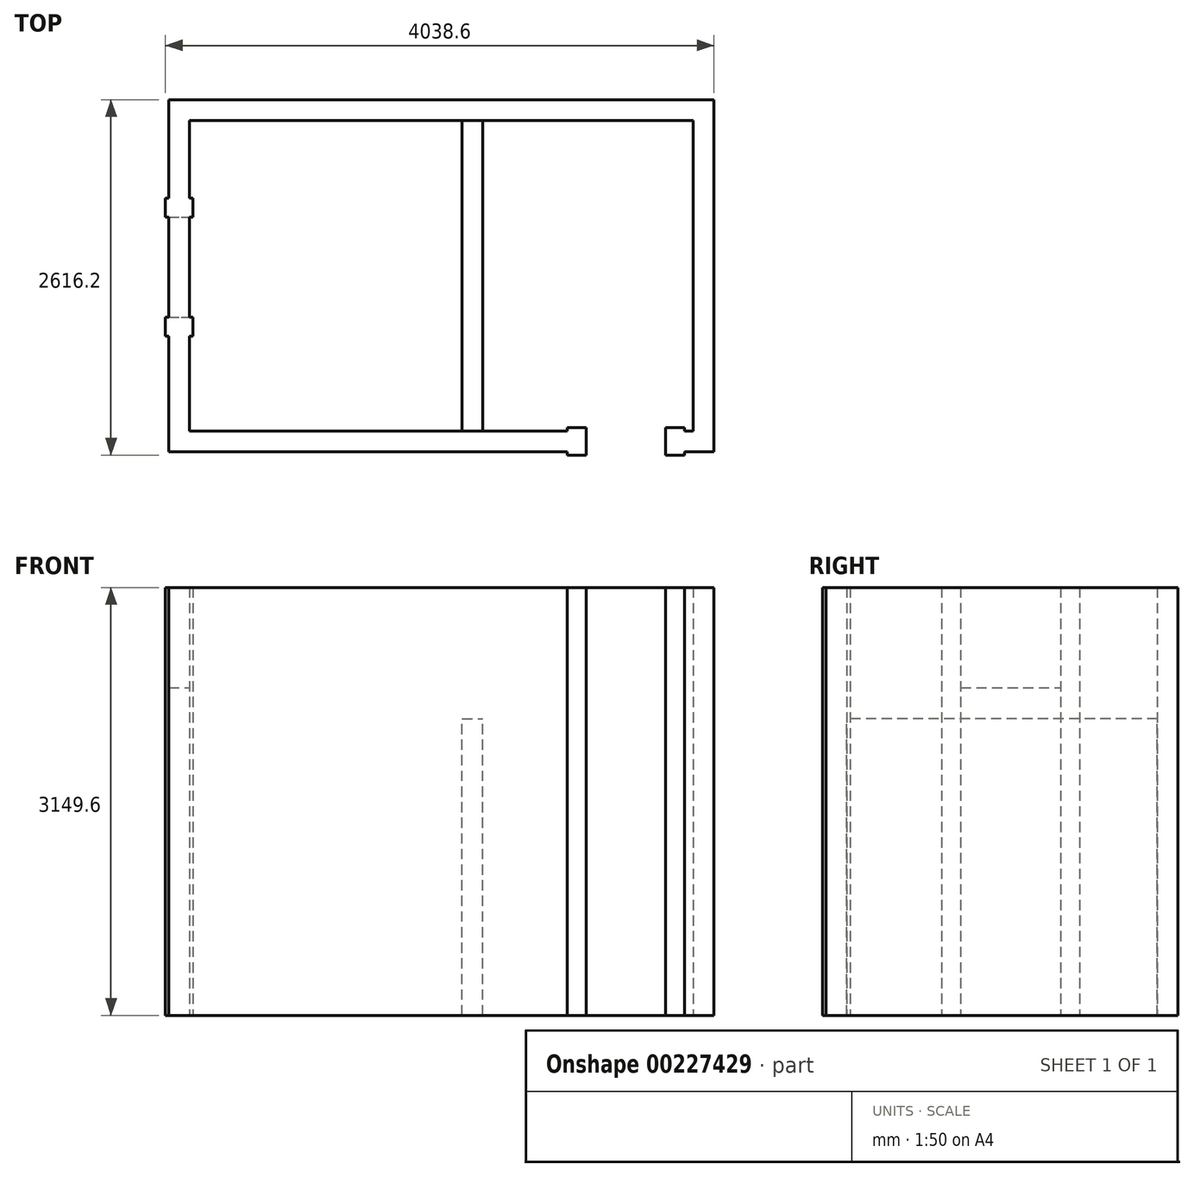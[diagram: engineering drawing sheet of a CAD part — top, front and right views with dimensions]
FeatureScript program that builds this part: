
annotation { "Feature Type Name" : "Feature", "Feature Type Description" : "" }
export const myFeature = defineFeature(function(context is Context, id is Id, definition is map)
    precondition{}
    {
        {
            var Q0;
            Q0=qCreatedBy(makeId("Top.planeOp"),FACE);
            var sketch = newSketch(context, id + "F0", { "sketchPlane" : qUnion([Q0])});
            skLineSegment(sketch, "E0.bottom", {"start": v(0, 0) * mm, "end": v(3708.4, 0) * mm});
            skLineSegment(sketch, "E0.top", {"start": v(0, 2286) * mm, "end": v(3708.4, 2286) * mm});
            skLineSegment(sketch, "E0.left", {"start": v(0, 0) * mm, "end": v(0, 2286) * mm});
            skLineSegment(sketch, "E0.right", {"start": v(3708.4, 0) * mm, "end": v(3708.4, 2286) * mm});
            skLineSegment(sketch, "E1.bottom", {"start": v(-152.4, -152.4) * mm, "end": v(3860.8, -152.4) * mm});
            skLineSegment(sketch, "E1.top", {"start": v(-152.4, 2438.4) * mm, "end": v(3860.8, 2438.4) * mm});
            skLineSegment(sketch, "E1.left", {"start": v(-152.4, -152.4) * mm, "end": v(-152.4, 2438.4) * mm});
            skLineSegment(sketch, "E1.right", {"start": v(3860.8, -152.4) * mm, "end": v(3860.8, 2438.4) * mm});
            skLineSegment(sketch, "E2.bottom", {"start": v(-152.4, 1574.8) * mm, "end": v(0, 1574.8) * mm});
            skLineSegment(sketch, "E2.top", {"start": v(-152.4, 838.2) * mm, "end": v(0, 838.2) * mm});
            skLineSegment(sketch, "E2.left", {"start": v(-152.4, 1574.8) * mm, "end": v(-152.4, 838.2) * mm});
            skLineSegment(sketch, "E2.right", {"start": v(0, 1574.8) * mm, "end": v(0, 838.2) * mm});
            skLineSegment(sketch, "E3.top", {"start": v(2921, -152.4) * mm, "end": v(3505.2, -152.4) * mm});
            skLineSegment(sketch, "E3.left", {"start": v(2921, 0) * mm, "end": v(2921, -152.4) * mm});
            skLineSegment(sketch, "E3.right", {"start": v(3505.2, 0) * mm, "end": v(3505.2, -152.4) * mm});
            skLineSegment(sketch, "E4.bottom", {"start": v(-177.8, 1714.5) * mm, "end": v(25.4, 1714.5) * mm});
            skLineSegment(sketch, "E4.top", {"start": v(-177.8, 1574.8) * mm, "end": v(25.4, 1574.8) * mm});
            skLineSegment(sketch, "E4.left", {"start": v(-177.8, 1714.5) * mm, "end": v(-177.8, 1574.8) * mm});
            skLineSegment(sketch, "E4.right", {"start": v(25.4, 1714.5) * mm, "end": v(25.4, 1574.8) * mm});
            skLineSegment(sketch, "E5.bottom", {"start": v(-177.8, 838.2) * mm, "end": v(25.4, 838.2) * mm});
            skLineSegment(sketch, "E5.top", {"start": v(-177.8, 698.5) * mm, "end": v(25.4, 698.5) * mm});
            skLineSegment(sketch, "E5.left", {"start": v(-177.8, 838.2) * mm, "end": v(-177.8, 698.5) * mm});
            skLineSegment(sketch, "E5.right", {"start": v(25.4, 838.2) * mm, "end": v(25.4, 698.5) * mm});
            skLineSegment(sketch, "E6.top", {"start": v(2692.4, 25.4) * mm, "end": v(2844.8, 25.4) * mm});
            skLineSegment(sketch, "E7.bottom", {"start": v(2781.3, 25.4) * mm, "end": v(2921, 25.4) * mm});
            skLineSegment(sketch, "E7.top", {"start": v(2781.3, -177.8) * mm, "end": v(2921, -177.8) * mm});
            skLineSegment(sketch, "E7.left", {"start": v(2781.3, 25.4) * mm, "end": v(2781.3, -177.8) * mm});
            skLineSegment(sketch, "E7.right", {"start": v(2921, 25.4) * mm, "end": v(2921, -177.8) * mm});
            skLineSegment(sketch, "E8.bottom", {"start": v(3505.2, 25.4) * mm, "end": v(3644.9, 25.4) * mm});
            skLineSegment(sketch, "E8.top", {"start": v(3505.2, -177.8) * mm, "end": v(3644.9, -177.8) * mm});
            skLineSegment(sketch, "E8.left", {"start": v(3505.2, 25.4) * mm, "end": v(3505.2, -177.8) * mm});
            skLineSegment(sketch, "E8.right", {"start": v(3644.9, 25.4) * mm, "end": v(3644.9, -177.8) * mm});
            skLineSegment(sketch, "E9", {"start": v(2006.6, 2286) * mm, "end": v(2006.6, 0) * mm});
            skLineSegment(sketch, "E10", {"start": v(2159, 2286) * mm, "end": v(2159, 0) * mm});
            skSolve(sketch);
        }
        {
            var Q0;
            {var subQ3=sQuery(id+"F0.wireOp",EDGE,"E0.top");Q0=makeQuery(id+"F0.imprint","IMPRINT",FACE,{"disambiguationData":[TD([[makeQuery(id+"F0.imprint","IMPRINT",EDGE,{"derivedFrom":subQ3}),1.0]])]});}
            var Q1;
            {var subQ3=sQuery(id+"F0.wireOp",EDGE,"E2.top");Q1=makeQuery(id+"F0.imprint","IMPRINT",FACE,{"disambiguationData":[TD([[makeQuery(id+"F0.imprint","IMPRINT",EDGE,{"derivedFrom":subQ3}),-1.0]])]});}
            var Q2;
            {var subQ5=sQuery(id+"F0.wireOp",EDGE,"E8.bottom");Q2=makeQuery(id+"F0.imprint","IMPRINT",FACE,{"disambiguationData":[TD([[makeQuery(id+"F0.imprint","IMPRINT",EDGE,{"derivedFrom":subQ5}),-1.0]])]});}
            var Q3;
            {var subQ0=sQuery(id+"F0.wireOp",EDGE,"E8.left");var subQ1=sQuery(id+"F0.wireOp",EDGE,"E0.bottom");var subQ2=makeQuery(id+"F0.imprint","INTERSECT",VERTEX,{"derivedFrom":[subQ1,subQ0]});Q3=makeQuery(id+"F0.imprint","IMPRINT",FACE,{"disambiguationData":[TD([[makeQuery(id+"F0.imprint","IMPRINT",EDGE,{"disambiguationData":[TD([[subQ2,-1.0]])],"derivedFrom":subQ1}),-1.0]])]});}
            var Q4;
            {var subQ5=sQuery(id+"F0.wireOp",EDGE,"E8.top");Q4=makeQuery(id+"F0.imprint","IMPRINT",FACE,{"disambiguationData":[TD([[makeQuery(id+"F0.imprint","IMPRINT",EDGE,{"derivedFrom":subQ5}),1.0]])]});}
            var Q5;
            {var subQ5=sQuery(id+"F0.wireOp",EDGE,"E7.top");Q5=makeQuery(id+"F0.imprint","IMPRINT",FACE,{"disambiguationData":[TD([[makeQuery(id+"F0.imprint","IMPRINT",EDGE,{"derivedFrom":subQ5}),1.0]])]});}
            var Q6;
            {var subQ0=sQuery(id+"F0.wireOp",EDGE,"E7.left");var subQ1=sQuery(id+"F0.wireOp",EDGE,"E0.bottom");var subQ2=makeQuery(id+"F0.imprint","INTERSECT",VERTEX,{"derivedFrom":[subQ1,subQ0]});Q6=makeQuery(id+"F0.imprint","IMPRINT",FACE,{"disambiguationData":[TD([[makeQuery(id+"F0.imprint","IMPRINT",EDGE,{"disambiguationData":[TD([[subQ2,-1.0]])],"derivedFrom":subQ1}),-1.0]])]});}
            var Q7;
            {var subQ1=sQuery(id+"F0.wireOp",EDGE,"E7.bottom");var subQ7=makeQuery(id+"F0.imprint","IMPRINT",VERTEX,{"derivedFrom":subQ1});Q7=makeQuery(id+"F0.imprint","IMPRINT",FACE,{"disambiguationData":[TD([[makeQuery(id+"F0.imprint","IMPRINT",EDGE,{"disambiguationData":[TD([[subQ7,1.0]])],"derivedFrom":subQ1}),-1.0]])]});}
            var Q8;
            {var subQ5=sQuery(id+"F0.wireOp",EDGE,"E0.left");var subQ6=sQuery(id+"F0.wireOp",EDGE,"E0.bottom");var subQ7=makeQuery(id+"F0.imprint","INTERSECT",VERTEX,{"derivedFrom":[subQ6,subQ5]});Q8=makeQuery(id+"F0.imprint","IMPRINT",FACE,{"disambiguationData":[TD([[makeQuery(id+"F0.imprint","IMPRINT",EDGE,{"disambiguationData":[TD([[subQ7,-1.0]])],"derivedFrom":subQ6}),-1.0]])]});}
            var Q9;
            {var subQ3=sQuery(id+"F0.wireOp",EDGE,"E5.top");var subQ5=sQuery(id+"F0.wireOp",EDGE,"E1.left");var subQ6=makeQuery(id+"F0.imprint","INTERSECT",VERTEX,{"derivedFrom":[subQ5,subQ3]});Q9=makeQuery(id+"F0.imprint","IMPRINT",FACE,{"disambiguationData":[TD([[makeQuery(id+"F0.imprint","IMPRINT",EDGE,{"disambiguationData":[TD([[subQ6,-1.0]])],"derivedFrom":subQ3}),1.0]])]});}
            var Q10;
            {var subQ5=sQuery(id+"F0.wireOp",EDGE,"E5.left");Q10=makeQuery(id+"F0.imprint","IMPRINT",FACE,{"disambiguationData":[TD([[makeQuery(id+"F0.imprint","IMPRINT",EDGE,{"derivedFrom":subQ5}),1.0]])]});}
            var Q11;
            {var subQ5=sQuery(id+"F0.wireOp",EDGE,"E4.right");Q11=makeQuery(id+"F0.imprint","IMPRINT",FACE,{"disambiguationData":[TD([[makeQuery(id+"F0.imprint","IMPRINT",EDGE,{"derivedFrom":subQ5}),-1.0]])]});}
            var Q12;
            {var subQ3=sQuery(id+"F0.wireOp",EDGE,"E4.bottom");var subQ5=sQuery(id+"F0.wireOp",EDGE,"E1.left");var subQ6=makeQuery(id+"F0.imprint","INTERSECT",VERTEX,{"derivedFrom":[subQ5,subQ3]});Q12=makeQuery(id+"F0.imprint","IMPRINT",FACE,{"disambiguationData":[TD([[makeQuery(id+"F0.imprint","IMPRINT",EDGE,{"disambiguationData":[TD([[subQ6,-1.0]])],"derivedFrom":subQ3}),-1.0]])]});}
            var Q13;
            {var subQ5=sQuery(id+"F0.wireOp",EDGE,"E4.left");Q13=makeQuery(id+"F0.imprint","IMPRINT",FACE,{"disambiguationData":[TD([[makeQuery(id+"F0.imprint","IMPRINT",EDGE,{"derivedFrom":subQ5}),1.0]])]});}
            var Q14;
            {var subQ5=sQuery(id+"F0.wireOp",EDGE,"E5.right");Q14=makeQuery(id+"F0.imprint","IMPRINT",FACE,{"disambiguationData":[TD([[makeQuery(id+"F0.imprint","IMPRINT",EDGE,{"derivedFrom":subQ5}),-1.0]])]});}
            extrude(context, id + "F1", {"entities" : qUnion([Q0, Q1, Q2, Q3, Q4, Q5, Q6, Q7, Q8, Q9, Q10, Q11, Q12, Q13, Q14]), "depth" : 2997.2 * mm});
        }
        {
            var Q0;
            Q0=makeQuery(id+"F0.imprint","IMPRINT",FACE,{"disambiguationData":[TD([[makeQuery(id+"F0.imprint","IMPRINT",EDGE,{"derivedFrom":sQuery(id+"F0.wireOp",EDGE,"E2.bottom")}),-1.0]])]});
            var Q1;
            Q1=makeQuery(id+"F0.imprint","IMPRINT",FACE,{"disambiguationData":[TD([[makeQuery(id+"F0.imprint","IMPRINT",EDGE,{"derivedFrom":sQuery(id+"F0.wireOp",EDGE,"E3.top")}),1.0]])]});
            var Q2;
            {var subQ0=sQuery(id+"F0.wireOp",EDGE,"E2.left");Q2=makeQuery(id+"F0.imprint","IMPRINT",FACE,{"disambiguationData":[TD([[makeQuery(id+"F0.imprint","IMPRINT",EDGE,{"derivedFrom":subQ0}),1.0]])]});}
            var Q3;
            Q3=makeQuery(id+"F1.opExtrude","CAP_FACE",FACE,{"disambiguationData":[OSD([sQuery(id+"F0.wireOp",EDGE,"E0.bottom"),sQuery(id+"F0.wireOp",EDGE,"E0.top"),sQuery(id+"F0.wireOp",EDGE,"E0.left"),sQuery(id+"F0.wireOp",EDGE,"E0.right"),sQuery(id+"F0.wireOp",EDGE,"E1.bottom"),sQuery(id+"F0.wireOp",EDGE,"E1.top"),sQuery(id+"F0.wireOp",EDGE,"E1.left"),sQuery(id+"F0.wireOp",EDGE,"E1.right"),sQuery(id+"F0.wireOp",EDGE,"E2.bottom"),sQuery(id+"F0.wireOp",EDGE,"E3.right")])],"isStart":false});
            var Q4;
            Q4=makeQuery(id+"F1.opExtrude","CAP_FACE",FACE,{"disambiguationData":[OSD([sQuery(id+"F0.wireOp",EDGE,"E0.bottom"),sQuery(id+"F0.wireOp",EDGE,"E0.top"),sQuery(id+"F0.wireOp",EDGE,"E0.left"),sQuery(id+"F0.wireOp",EDGE,"E0.right"),sQuery(id+"F0.wireOp",EDGE,"E1.bottom"),sQuery(id+"F0.wireOp",EDGE,"E1.top"),sQuery(id+"F0.wireOp",EDGE,"E1.left"),sQuery(id+"F0.wireOp",EDGE,"E1.right"),sQuery(id+"F0.wireOp",EDGE,"E2.bottom"),sQuery(id+"F0.wireOp",EDGE,"E3.right")])],"isStart":false});
            extrude(context, id + "F2", {"entities" : qUnion([Q0, Q1, Q2]), "operationType" : NewBodyOperationType.ADD, "endBound" : BoundingType.UP_TO_SURFACE, "endBoundEntityFace" : qUnion([Q3]), "depth" : 25.4 * mm, "hasSecondDirection" : true, "secondDirectionOppositeDirection" : false, "secondDirectionBoundEntityFace" : qUnion([Q4]), "secondDirectionDepth" : 2260.6 * mm});
        }
        {
            var Q0;
            {var subQ5=sQuery(id+"F0.wireOp",EDGE,"E8.bottom");Q0=makeQuery(id+"F0.imprint","IMPRINT",FACE,{"disambiguationData":[TD([[makeQuery(id+"F0.imprint","IMPRINT",EDGE,{"derivedFrom":subQ5}),-1.0]])]});}
            var Q1;
            {var subQ0=sQuery(id+"F0.wireOp",EDGE,"E8.left");var subQ1=sQuery(id+"F0.wireOp",EDGE,"E0.bottom");var subQ2=makeQuery(id+"F0.imprint","INTERSECT",VERTEX,{"derivedFrom":[subQ1,subQ0]});Q1=makeQuery(id+"F0.imprint","IMPRINT",FACE,{"disambiguationData":[TD([[makeQuery(id+"F0.imprint","IMPRINT",EDGE,{"disambiguationData":[TD([[subQ2,-1.0]])],"derivedFrom":subQ1}),-1.0]])]});}
            var Q2;
            {var subQ7=sQuery(id+"F0.wireOp",EDGE,"E0.top");Q2=makeQuery(id+"F0.imprint","IMPRINT",FACE,{"disambiguationData":[TD([[makeQuery(id+"F0.imprint","IMPRINT",EDGE,{"derivedFrom":subQ7}),1.0]])]});}
            var Q3;
            {var subQ5=sQuery(id+"F0.wireOp",EDGE,"E8.top");Q3=makeQuery(id+"F0.imprint","IMPRINT",FACE,{"disambiguationData":[TD([[makeQuery(id+"F0.imprint","IMPRINT",EDGE,{"derivedFrom":subQ5}),1.0]])]});}
            var Q4;
            {var subQ1=sQuery(id+"F0.wireOp",EDGE,"E7.bottom");var subQ7=makeQuery(id+"F0.imprint","IMPRINT",VERTEX,{"derivedFrom":subQ1});Q4=makeQuery(id+"F0.imprint","IMPRINT",FACE,{"disambiguationData":[TD([[makeQuery(id+"F0.imprint","IMPRINT",EDGE,{"disambiguationData":[TD([[subQ7,1.0]])],"derivedFrom":subQ1}),-1.0]])]});}
            var Q5;
            {var subQ5=sQuery(id+"F0.wireOp",EDGE,"E0.left");var subQ6=sQuery(id+"F0.wireOp",EDGE,"E0.bottom");var subQ7=makeQuery(id+"F0.imprint","INTERSECT",VERTEX,{"derivedFrom":[subQ6,subQ5]});Q5=makeQuery(id+"F0.imprint","IMPRINT",FACE,{"disambiguationData":[TD([[makeQuery(id+"F0.imprint","IMPRINT",EDGE,{"disambiguationData":[TD([[subQ7,-1.0]])],"derivedFrom":subQ6}),-1.0]])]});}
            var Q6;
            {var subQ0=sQuery(id+"F0.wireOp",EDGE,"E7.left");var subQ1=sQuery(id+"F0.wireOp",EDGE,"E0.bottom");var subQ2=makeQuery(id+"F0.imprint","INTERSECT",VERTEX,{"derivedFrom":[subQ1,subQ0]});Q6=makeQuery(id+"F0.imprint","IMPRINT",FACE,{"disambiguationData":[TD([[makeQuery(id+"F0.imprint","IMPRINT",EDGE,{"disambiguationData":[TD([[subQ2,-1.0]])],"derivedFrom":subQ1}),-1.0]])]});}
            var Q7;
            {var subQ5=sQuery(id+"F0.wireOp",EDGE,"E7.top");Q7=makeQuery(id+"F0.imprint","IMPRINT",FACE,{"disambiguationData":[TD([[makeQuery(id+"F0.imprint","IMPRINT",EDGE,{"derivedFrom":subQ5}),1.0]])]});}
            var Q8;
            {var subQ5=sQuery(id+"F0.wireOp",EDGE,"E5.right");Q8=makeQuery(id+"F0.imprint","IMPRINT",FACE,{"disambiguationData":[TD([[makeQuery(id+"F0.imprint","IMPRINT",EDGE,{"derivedFrom":subQ5}),-1.0]])]});}
            var Q9;
            {var subQ3=sQuery(id+"F0.wireOp",EDGE,"E5.top");var subQ5=sQuery(id+"F0.wireOp",EDGE,"E1.left");var subQ6=makeQuery(id+"F0.imprint","INTERSECT",VERTEX,{"derivedFrom":[subQ5,subQ3]});Q9=makeQuery(id+"F0.imprint","IMPRINT",FACE,{"disambiguationData":[TD([[makeQuery(id+"F0.imprint","IMPRINT",EDGE,{"disambiguationData":[TD([[subQ6,-1.0]])],"derivedFrom":subQ3}),1.0]])]});}
            var Q10;
            {var subQ5=sQuery(id+"F0.wireOp",EDGE,"E5.left");Q10=makeQuery(id+"F0.imprint","IMPRINT",FACE,{"disambiguationData":[TD([[makeQuery(id+"F0.imprint","IMPRINT",EDGE,{"derivedFrom":subQ5}),1.0]])]});}
            var Q11;
            {var subQ3=sQuery(id+"F0.wireOp",EDGE,"E4.bottom");var subQ5=sQuery(id+"F0.wireOp",EDGE,"E1.left");var subQ6=makeQuery(id+"F0.imprint","INTERSECT",VERTEX,{"derivedFrom":[subQ5,subQ3]});Q11=makeQuery(id+"F0.imprint","IMPRINT",FACE,{"disambiguationData":[TD([[makeQuery(id+"F0.imprint","IMPRINT",EDGE,{"disambiguationData":[TD([[subQ6,-1.0]])],"derivedFrom":subQ3}),-1.0]])]});}
            var Q12;
            {var subQ5=sQuery(id+"F0.wireOp",EDGE,"E4.right");Q12=makeQuery(id+"F0.imprint","IMPRINT",FACE,{"disambiguationData":[TD([[makeQuery(id+"F0.imprint","IMPRINT",EDGE,{"derivedFrom":subQ5}),-1.0]])]});}
            var Q13;
            {var subQ14=sQuery(id+"F0.wireOp",EDGE,"E0.top");Q13=makeQuery(id+"F0.imprint","IMPRINT",FACE,{"disambiguationData":[TD([[makeQuery(id+"F0.imprint","IMPRINT",EDGE,{"derivedFrom":subQ14}),-1.0]])]});}
            var Q14;
            {var subQ5=sQuery(id+"F0.wireOp",EDGE,"E4.left");Q14=makeQuery(id+"F0.imprint","IMPRINT",FACE,{"disambiguationData":[TD([[makeQuery(id+"F0.imprint","IMPRINT",EDGE,{"derivedFrom":subQ5}),1.0]])]});}
            var Q15;
            {var subQ0=sQuery(id+"F0.wireOp",EDGE,"E2.left");Q15=makeQuery(id+"F0.imprint","IMPRINT",FACE,{"disambiguationData":[TD([[makeQuery(id+"F0.imprint","IMPRINT",EDGE,{"derivedFrom":subQ0}),1.0]])]});}
            var Q16;
            {var subQ5=sQuery(id+"F0.wireOp",EDGE,"E3.top");Q16=makeQuery(id+"F0.imprint","IMPRINT",FACE,{"disambiguationData":[TD([[makeQuery(id+"F0.imprint","IMPRINT",EDGE,{"derivedFrom":subQ5}),1.0]])]});}
            extrude(context, id + "F3", {"entities" : qUnion([Q0, Q1, Q2, Q3, Q4, Q5, Q6, Q7, Q8, Q9, Q10, Q11, Q12, Q13, Q14, Q15, Q16]), "operationType" : NewBodyOperationType.ADD, "oppositeDirection" : true, "depth" : 152.4 * mm});
        }
        {
            var Q0;
            {var subQ0=sQuery(id+"F0.wireOp",EDGE,"E9");Q0=makeQuery(id+"F0.imprint","IMPRINT",FACE,{"disambiguationData":[TD([[makeQuery(id+"F0.imprint","IMPRINT",EDGE,{"derivedFrom":subQ0}),1.0]])]});}
            extrude(context, id + "F4", {"entities" : qUnion([Q0]), "operationType" : NewBodyOperationType.ADD, "depth" : 2032 * mm});
        }
    });
